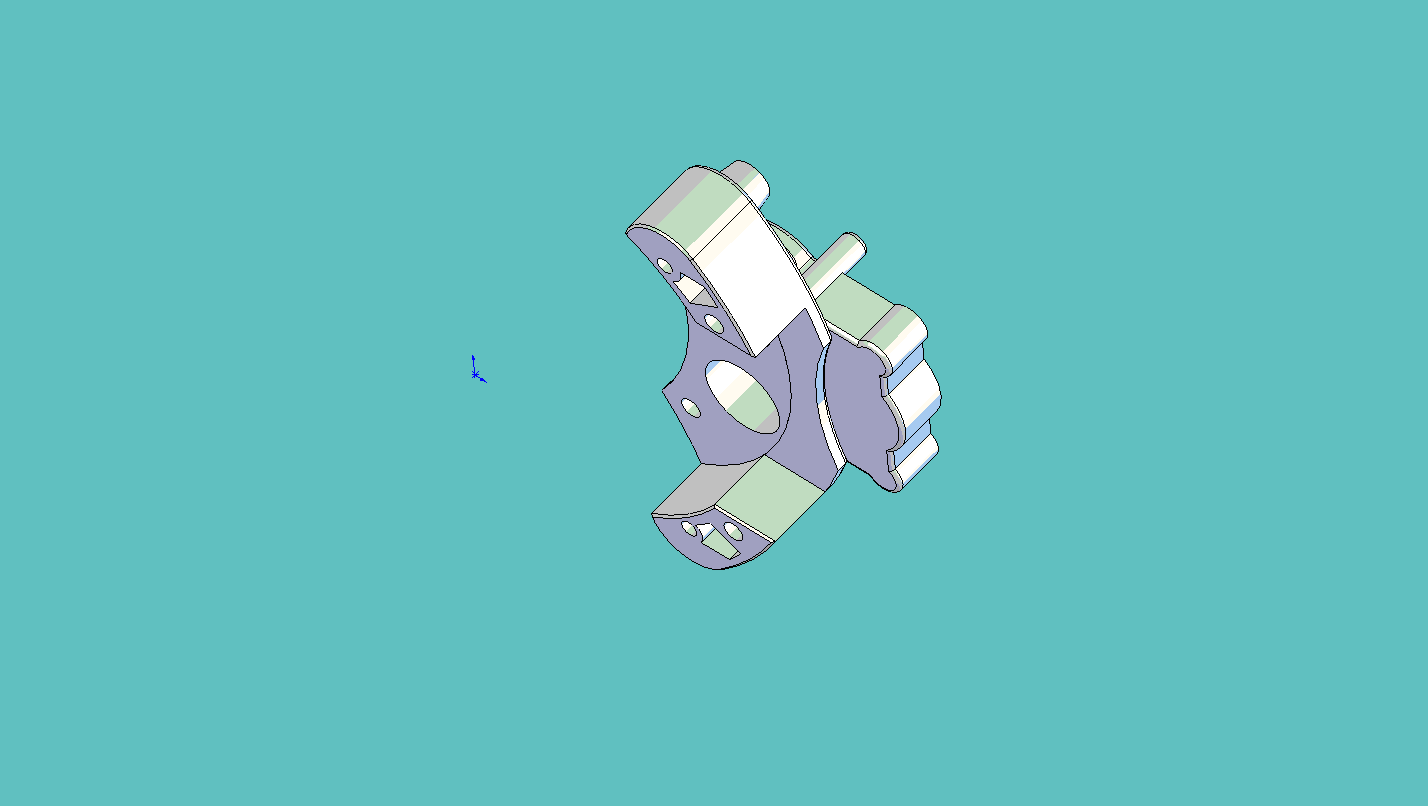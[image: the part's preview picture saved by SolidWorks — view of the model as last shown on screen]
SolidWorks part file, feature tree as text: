
SOLIDWORKS PART (.sldprt)
format: sldprt  version: not decoded by parser v0  size: 2,041,344 bytes
history: native  units: mm
features: sketch x22, cut_extrude x15, fillet x10, extrude x7, plane x2, material x1, chamfer x1, mirror x1, delete_body x1 (+14 scaffold rows collapsed)
feature tree (74):
  scaffold x14  (default folders/planes/origin — collapsed)
  material  "Material <not specified>"
  sketch  "Sketch1"  dims[D1=63.5mm]
  extrude  "Extrude1"  Depth=31.75mm
  sketch  "Sketch5"  dims[D1=~43.962388mm]
  extrude  "Extrude2"  Depth=50.8mm
  sketch  "Sketch3"  dims[D1=50.0mm]
  cut_extrude  "Cut-Extrude1"  Depth=25.4mm
  sketch  "Sketch7"  dims[c1.D1=12.7mm c1.D2=12.7mm c2.D1=~13.906952mm c2.D2=25.0mm c2.D3=25.0mm c3.D1=~12.799272mm c3.D3=152.4mm]
  fillet  "Fillet1"  Radius=2.54mm
  fillet  "Fillet2"  Radius=2.54mm
  fillet  "Fillet3"  Radius=2.54mm
  sketch  "Sketch10"
  cut_extrude  "Cut-Extrude3"  [1 undecoded]
  plane  "Plane1"  Offset=10.16mm
  plane  "Plane2"  Offset=8.636mm
  sketch  "Sketch13"  dims[D1=273.05mm D2=137.16mm]
  cut_extrude  "Cut-Extrude4"  [1 undecoded]
  sketch  "Sketch14"
  cut_extrude  "Cut-Extrude5"  [1 undecoded]
  sketch  "Sketch15"
  extrude  "Extrude3"  Depth=53.18mm
  fillet  "Fillet4"  Radius=2.54mm
  sketch  "Sketch16"  dims[D1=~1.636236mm]
  cut_extrude  "Cut-Extrude6"  Depth=27.94mm
  fillet  "Fillet5"  Radius=2.54mm
  sketch  "Sketch17"
  extrude  "Extrude4"  Depth=2.54mm
  fillet  "Fillet6"  Radius=0.508mm
  chamfer  "Chamfer1"  Distance=1.27mm Angle=45deg
  sketch  "Sketch20"  dims[c1.D1=31.75mm c1.D2=25.4mm c2.D1=~20.003376mm]
  extrude  "Extrude5"  Depth=20.32mm
  cut_extrude  "Cut-Extrude8"  [1 undecoded]
  sketch  "Sketch21"  dims[D1=~4.108238mm]
  cut_extrude  "Cut-Extrude10"  Depth=25.4mm
  fillet  "Fillet7"  Radius=2.54mm
  sketch  "Sketch22"  dims[D1=10.16mm]
  cut_extrude  "Cut-Extrude11"  [1 undecoded]
  sketch  "Sketch24"
  cut_extrude  "Cut-Extrude12"  Depth=22.86mm
  sketch  "Sketch25"  dims[D1=20.574mm]
  extrude  "Extrude6"  Depth=5.08mm
  fillet  "Fillet8"  Radius=2.54mm
  sketch  "Sketch27"  dims[D1=~16.253517mm]
  cut_extrude  "Cut-Extrude15"  Depth=5.08mm
  sketch  "Sketch28"
  cut_extrude  "Cut-Extrude16"  Depth=2.54mm
  fillet  "Fillet9"  Radius=0.762mm
  mirror  "Mirror1"
  sketch  "Sketch29"  dims[D1=7.62mm]
  extrude  "Extrude7"  [1 undecoded]
  sketch  "Sketch30"
  sketch  "Sketch31"  dims[D1=5.08mm]
  cut_extrude  "Cut-Extrude18"  Depth=16.392582mm
  sketch  "Sketch32"  dims[D1=8.89mm]
  cut_extrude  "Cut-Extrude19"  Depth=16.392582mm
  cut_extrude  "Cut-Extrude20"  Depth=43.688mm
  sketch  "Sketch33"
  cut_extrude  "Cut-Extrude21"  Depth=59.69mm
  fillet  "Fillet11"  Radius=2.54mm
  delete_body  "Body-Delete1"
decode coverage: 41 of 57 modeling features carry decoded parameters
note: ~ marks probable driven/reference dimensions
note: 6 parameter values undecoded
summary: no parameter record found for 6 features
note: suppression state not decoded; provenance and decode notes live in map.json
